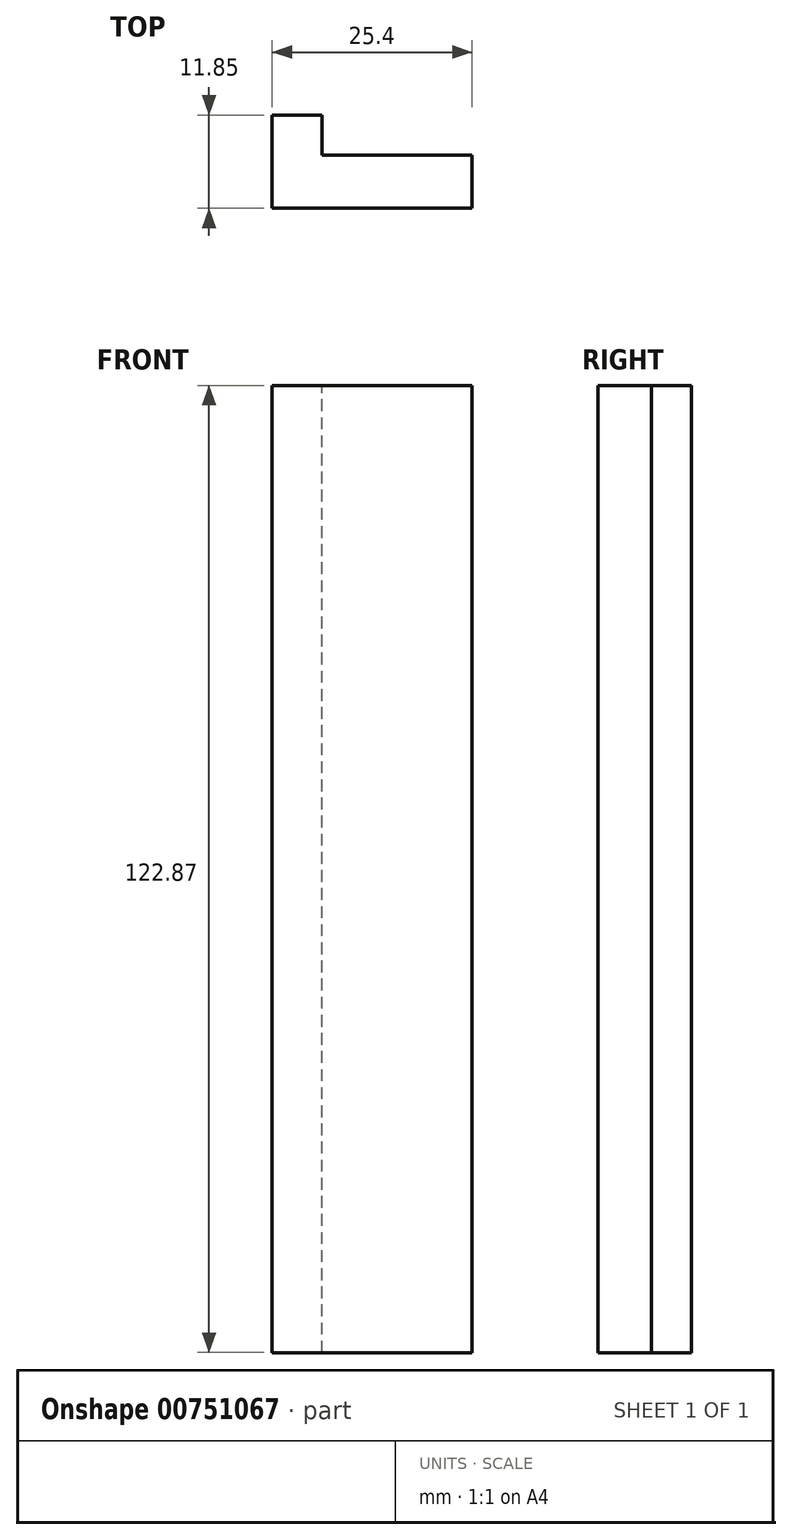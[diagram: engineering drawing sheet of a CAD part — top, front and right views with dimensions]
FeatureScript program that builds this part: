
annotation { "Feature Type Name" : "Feature", "Feature Type Description" : "" }
export const myFeature = defineFeature(function(context is Context, id is Id, definition is map)
    precondition{}
    {
        {
            var Q0;
            Q0=qCreatedBy(makeId("Right.planeOp"),FACE);
            var sketch = newSketch(context, id + "F0", { "sketchPlane" : qUnion([Q0])});
            skLineSegment(sketch, "E0.bottom", {"start": v(48.17, -58.76) * mm, "end": v(41.4, -58.76) * mm});
            skLineSegment(sketch, "E0.top", {"start": v(48.17, 64.11) * mm, "end": v(41.4, 64.11) * mm});
            skLineSegment(sketch, "E0.left", {"start": v(48.17, -58.76) * mm, "end": v(48.17, 64.11) * mm});
            skLineSegment(sketch, "E0.right", {"start": v(41.4, -58.76) * mm, "end": v(41.4, 64.11) * mm});
            skSolve(sketch);
        }
        {
            var Q0;
            Q0 = qSketchRegion(id + "F0", true);
            extrude(context, id + "F1", {"entities" : qUnion([Q0]), "depth" : 25.4 * mm, "offsetDistance" : 25.4 * mm});
        }
        {
            var Q0;
            Q0=makeQuery(id+"F1.opExtrude","SWEPT_FACE",FACE,{"disambiguationData":[OSD([sQuery(id+"F0.wireOp",EDGE,"E0.left")])]});
            var sketch = newSketch(context, id + "F2", { "sketchPlane" : qUnion([Q0])});
            skLineSegment(sketch, "E1.bottom", {"start": v(0, -58.76) * mm, "end": v(-6.34, -58.76) * mm});
            skLineSegment(sketch, "E1.top", {"start": v(0, 64.11) * mm, "end": v(-6.34, 64.11) * mm});
            skLineSegment(sketch, "E1.left", {"start": v(0, -58.76) * mm, "end": v(0, 64.11) * mm});
            skLineSegment(sketch, "E1.right", {"start": v(-6.34, -58.76) * mm, "end": v(-6.34, 64.11) * mm});
            skSolve(sketch);
        }
        {
            var Q0;
            Q0=makeQuery(id+"F2.imprint","IMPRINT",FACE,{"disambiguationData":[TD([[makeQuery(id+"F2.imprint","IMPRINT",EDGE,{"derivedFrom":sQuery(id+"F2.wireOp",EDGE,"E1.bottom")}),1.0]])]});
            extrude(context, id + "F3", {"entities" : qUnion([Q0]), "operationType" : NewBodyOperationType.ADD, "depth" : 5.08 * mm, "offsetDistance" : 25.4 * mm});
        }
    });
